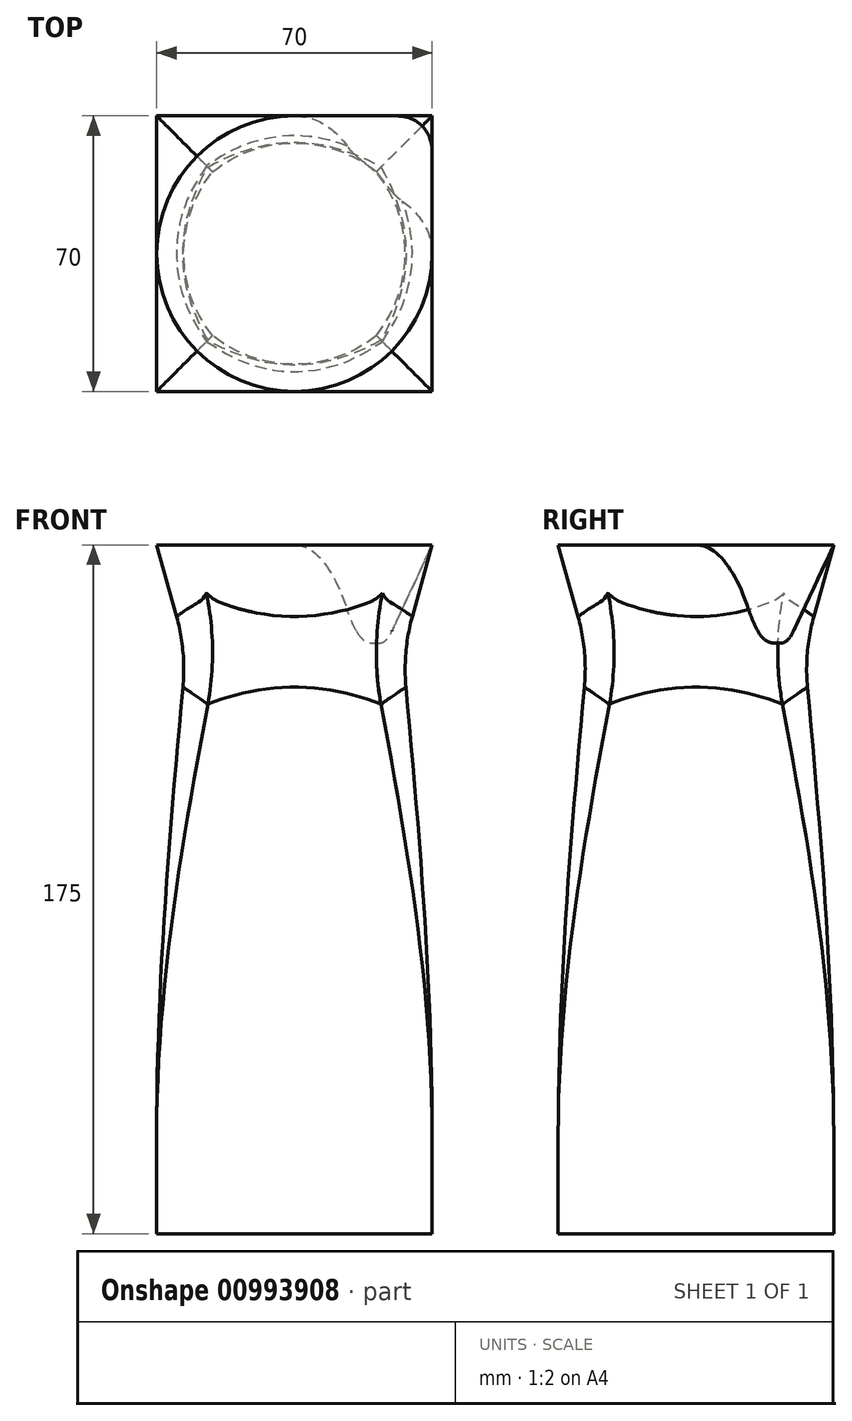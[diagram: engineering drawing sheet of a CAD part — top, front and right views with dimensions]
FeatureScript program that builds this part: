
annotation { "Feature Type Name" : "Feature", "Feature Type Description" : "" }
export const myFeature = defineFeature(function(context is Context, id is Id, definition is map)
    precondition{}
    {
        {
            var Q0;
            Q0=qCreatedBy(makeId("Top.planeOp"),FACE);
            var sketch = newSketch(context, id + "F0", { "sketchPlane" : qUnion([Q0])});
            skLineSegment(sketch, "E0", {"start": v(35, 35) * mm, "end": v(35, -35) * mm});
            skLineSegment(sketch, "E1", {"start": v(35, -35) * mm, "end": v(-35, -35) * mm});
            skLineSegment(sketch, "E2", {"start": v(-35, -35) * mm, "end": v(-35, 35) * mm});
            skLineSegment(sketch, "E3", {"start": v(-35, 35) * mm, "end": v(35, 35) * mm});
            skSolve(sketch);
        }
        {
            var Q0;
            Q0=qCreatedBy(makeId("Top.planeOp"),FACE);
            cPlane(context, id + "F1", {"entities" : qUnion([Q0]), "cplaneType" : CPlaneType.OFFSET, "offset" : 150 * mm, "width" : 150 * mm, "height" : 150 * mm});
        }
        {
            var Q0;
            Q0=qCreatedBy(id+"F1.planeOp",FACE);
            var sketch = newSketch(context, id + "F2", { "sketchPlane" : qUnion([Q0])});
            skCircle(sketch, "E4", {"center": v(0, 0) * mm, "radius": 35 * mm});
            skSolve(sketch);
        }
        {
            var Q0;
            Q0=qCreatedBy(id+"F1.planeOp",FACE);
            cPlane(context, id + "F3", {"entities" : qUnion([Q0]), "cplaneType" : CPlaneType.OFFSET, "offset" : 27 * mm, "oppositeDirection" : true, "width" : 150 * mm, "height" : 150 * mm});
        }
        {
            var Q0;
            Q0=qCreatedBy(id+"F3.planeOp",FACE);
            var sketch = newSketch(context, id + "F4", { "sketchPlane" : qUnion([Q0])});
            skCircle(sketch, "E5", {"center": v(0, 0) * mm, "radius": 27.5 * mm});
            skSolve(sketch);
        }
        {
            var Q0;
            Q0=makeQuery(id+"F0.imprint","IMPRINT",FACE,{"disambiguationData":[TD([[makeQuery(id+"F0.imprint","IMPRINT",EDGE,{"derivedFrom":sQuery(id+"F0.wireOp",EDGE,"E0")}),-1.0]])]});
            var Q1;
            Q1=makeQuery(id+"F4.imprint","IMPRINT",FACE,{"disambiguationData":[TD([[makeQuery(id+"F4.imprint","IMPRINT",EDGE,{"derivedFrom":sQuery(id+"F4.wireOp",EDGE,"E5")}),1.0]])]});
            loft(context, id + "F5", {"startCondition" : LoftEndDerivativeType.NORMAL_TO_PROFILE, "startMagnitude" : 1, "sheetProfilesArray" : [{ "sheetProfileEntities" : qUnion([Q0]) }, { "sheetProfileEntities" : qUnion([Q1]) }]});
        }
        {
            var Q1;
            Q1=makeQuery(id+"F5.opLoft","CAP_FACE",FACE,{"disambiguationData":[OSD([makeQuery(id+"F4.imprint","IMPRINT",FACE,{"disambiguationData":[TD([[makeQuery(id+"F4.imprint","IMPRINT",EDGE,{"derivedFrom":sQuery(id+"F4.wireOp",EDGE,"E5")}),1.0]])]})])],"isStart":true});
            var Q2;
            Q2=makeQuery(id+"F2.imprint","IMPRINT",FACE,{"disambiguationData":[TD([[makeQuery(id+"F2.imprint","IMPRINT",EDGE,{"derivedFrom":sQuery(id+"F2.wireOp",EDGE,"E4")}),1.0]])]});
            loft(context, id + "F6", {"operationType" : NewBodyOperationType.ADD, "sheetProfilesArray" : [{ "sheetProfileEntities" : qUnion([Q1]) }, { "sheetProfileEntities" : qUnion([Q2]) }]});
        }
        {
            var Q0;
            {var subQ0=sQuery(id+"F4.wireOp",EDGE,"E5");var subQ1=sQuery(id+"F0.wireOp",EDGE,"E3");var subQ2=sQuery(id+"F0.wireOp",EDGE,"E2");var subQ3=sQuery(id+"F0.wireOp",EDGE,"E1");var subQ4=sQuery(id+"F0.wireOp",EDGE,"E0");Q0=makeQuery(id+"F6.boolean.opBoolean","MERGE",EDGE,{"derivedFrom":[makeQuery(id+"F5.opLoft","MID_CAP_EDGE",EDGE,{"disambiguationData":[OSD([subQ4,subQ3,subQ2,subQ1,subQ0])],"capPos":1.0}),makeQuery(id+"F6.opLoft","MID_CAP_EDGE",EDGE,{"disambiguationData":[OSD([subQ4,subQ3,subQ2,subQ1,subQ0])],"capPos":0.0})]});}
            var Q1;
            {var subQ0=sQuery(id+"F4.wireOp",EDGE,"E5");var subQ1=sQuery(id+"F0.wireOp",EDGE,"E3");var subQ2=sQuery(id+"F0.wireOp",EDGE,"E0");Q1=makeQuery(id+"F6.boolean.opBoolean","MERGE",EDGE,{"derivedFrom":[makeQuery(id+"F5.opLoft","MID_CAP_EDGE",EDGE,{"disambiguationData":[OSD([subQ2,subQ1,subQ0])],"capPos":1.0}),makeQuery(id+"F6.opLoft","MID_CAP_EDGE",EDGE,{"disambiguationData":[OSD([subQ2,subQ1,subQ0])],"capPos":0.0})]});}
            var Q2;
            {var subQ0=sQuery(id+"F4.wireOp",EDGE,"E5");var subQ1=sQuery(id+"F0.wireOp",EDGE,"E3");var subQ2=sQuery(id+"F0.wireOp",EDGE,"E2");var subQ3=sQuery(id+"F0.wireOp",EDGE,"E0");Q2=makeQuery(id+"F6.boolean.opBoolean","MERGE",EDGE,{"derivedFrom":[makeQuery(id+"F5.opLoft","MID_CAP_EDGE",EDGE,{"disambiguationData":[OSD([subQ3,subQ2,subQ1,subQ0])],"capPos":1.0}),makeQuery(id+"F6.opLoft","MID_CAP_EDGE",EDGE,{"disambiguationData":[OSD([subQ3,subQ2,subQ1,subQ0])],"capPos":0.0})]});}
            var Q3;
            {var subQ0=sQuery(id+"F4.wireOp",EDGE,"E5");var subQ1=sQuery(id+"F0.wireOp",EDGE,"E3");var subQ2=sQuery(id+"F0.wireOp",EDGE,"E2");var subQ3=sQuery(id+"F0.wireOp",EDGE,"E1");Q3=makeQuery(id+"F6.boolean.opBoolean","MERGE",EDGE,{"derivedFrom":[makeQuery(id+"F5.opLoft","MID_CAP_EDGE",EDGE,{"disambiguationData":[OSD([subQ3,subQ2,subQ1,subQ0])],"capPos":1.0}),makeQuery(id+"F6.opLoft","MID_CAP_EDGE",EDGE,{"disambiguationData":[OSD([subQ3,subQ2,subQ1,subQ0])],"capPos":0.0})]});}
            fillet(context, id + "F7", {"entities" : qUnion([Q0, Q1, Q2, Q3]), "radius" : 50 * mm, "tangentPropagation" : true, "allowEdgeOverflow" : false});
        }
        {
            var Q0;
            Q0=qCreatedBy(id+"F1.planeOp",FACE);
            var sketch = newSketch(context, id + "F8", { "sketchPlane" : qUnion([Q0])});
            skLineSegment(sketch, "E6", {"start": v(35, 0) * mm, "end": v(35, 35) * mm});
            skLineSegment(sketch, "E7", {"start": v(0, 35) * mm, "end": v(35, 35) * mm});
            skPoint(sketch, "E8.center.orphan", {"position": v(0, 0) * mm});
            skArc(sketch, "E9", {"start": v(0, 35) * mm, "mid": v(-5.96, 34.49) * mm, "end": v(-11.75, 32.97) * mm});
            skLineSegment(sketch, "E10", {"start": v(10.6, 10.6) * mm, "end": v(-11.75, 32.97) * mm});
            skLineSegment(sketch, "E11", {"start": v(-11.75, 32.97) * mm, "end": v(32.97, -11.75) * mm});
            skArc(sketch, "E12.trimOffspring", {"start": v(32.97, -11.75) * mm, "mid": v(34.49, -5.96) * mm, "end": v(35, 0) * mm});
            skSolve(sketch);
        }
        {
            var Q0;
            Q0=makeQuery(id+"F8.imprint","IMPRINT",FACE,{"disambiguationData":[TD([[makeQuery(id+"F8.imprint","IMPRINT",EDGE,{"derivedFrom":sQuery(id+"F8.wireOp",EDGE,"E6")}),1.0]])]});
            extrude(context, id + "F9", {"entities" : qUnion([Q0]), "operationType" : NewBodyOperationType.ADD, "oppositeDirection" : true, "depth" : 50 * mm, "offsetDistance" : 25 * mm, "hasDraft" : true, "draftAngle" : 25 * degree, "draftPullDirection" : true});
        }
        {
            var Q0;
            Q0=makeQuery(id+"F9.opExtrude","SWEPT_EDGE",EDGE,{"disambiguationData":[OSD([sQuery(id+"F8.wireOp",EDGE,"E6"),sQuery(id+"F8.wireOp",EDGE,"E7")])]});
            fillet(context, id + "F10", {"entities" : qUnion([Q0]), "radius" : 10 * mm, "tangentPropagation" : true, "allowEdgeOverflow" : false});
        }
        {
            var Q0;
            Q0=makeQuery(id+"F9.boolean.opBoolean","MERGE",FACE,{"derivedFrom":[makeQuery(id+"F6.opLoft","CAP_FACE",FACE,{"disambiguationData":[OSD([makeQuery(id+"F2.imprint","IMPRINT",FACE,{"disambiguationData":[TD([[makeQuery(id+"F2.imprint","IMPRINT",EDGE,{"derivedFrom":sQuery(id+"F2.wireOp",EDGE,"E4")}),1.0]])]})])],"isStart":true}),makeQuery(id+"F9.opExtrude","CAP_FACE",FACE,{"disambiguationData":[OSD([sQuery(id+"F8.wireOp",EDGE,"E6"),sQuery(id+"F8.wireOp",EDGE,"E7"),sQuery(id+"F8.wireOp",EDGE,"E9"),sQuery(id+"F8.wireOp",EDGE,"E11"),sQuery(id+"F8.wireOp",EDGE,"E12.trimOffspring")])],"isStart":true})]});
            var sketch = newSketch(context, id + "F11", { "sketchPlane" : qUnion([Q0])});
            skCircle(sketch, "E13", {"center": v(26.14, 26.14) * mm, "radius": 8.5 * mm});
            skLineSegment(sketch, "E14", {"start": v(0, 0) * mm, "end": v(-18.24, 18.24) * mm});
            skSolve(sketch);
        }
        {
            var Q0;
            Q0=makeQuery(id+"F5.opLoft","CAP_FACE",FACE,{"disambiguationData":[OSD([makeQuery(id+"F0.imprint","IMPRINT",FACE,{"disambiguationData":[TD([[makeQuery(id+"F0.imprint","IMPRINT",EDGE,{"derivedFrom":sQuery(id+"F0.wireOp",EDGE,"E0")}),-1.0]])]})])],"isStart":true});
            extrude(context, id + "F12", {"entities" : qUnion([Q0]), "operationType" : NewBodyOperationType.ADD, "depth" : 25 * mm, "offsetDistance" : 25 * mm});
        }
    });
